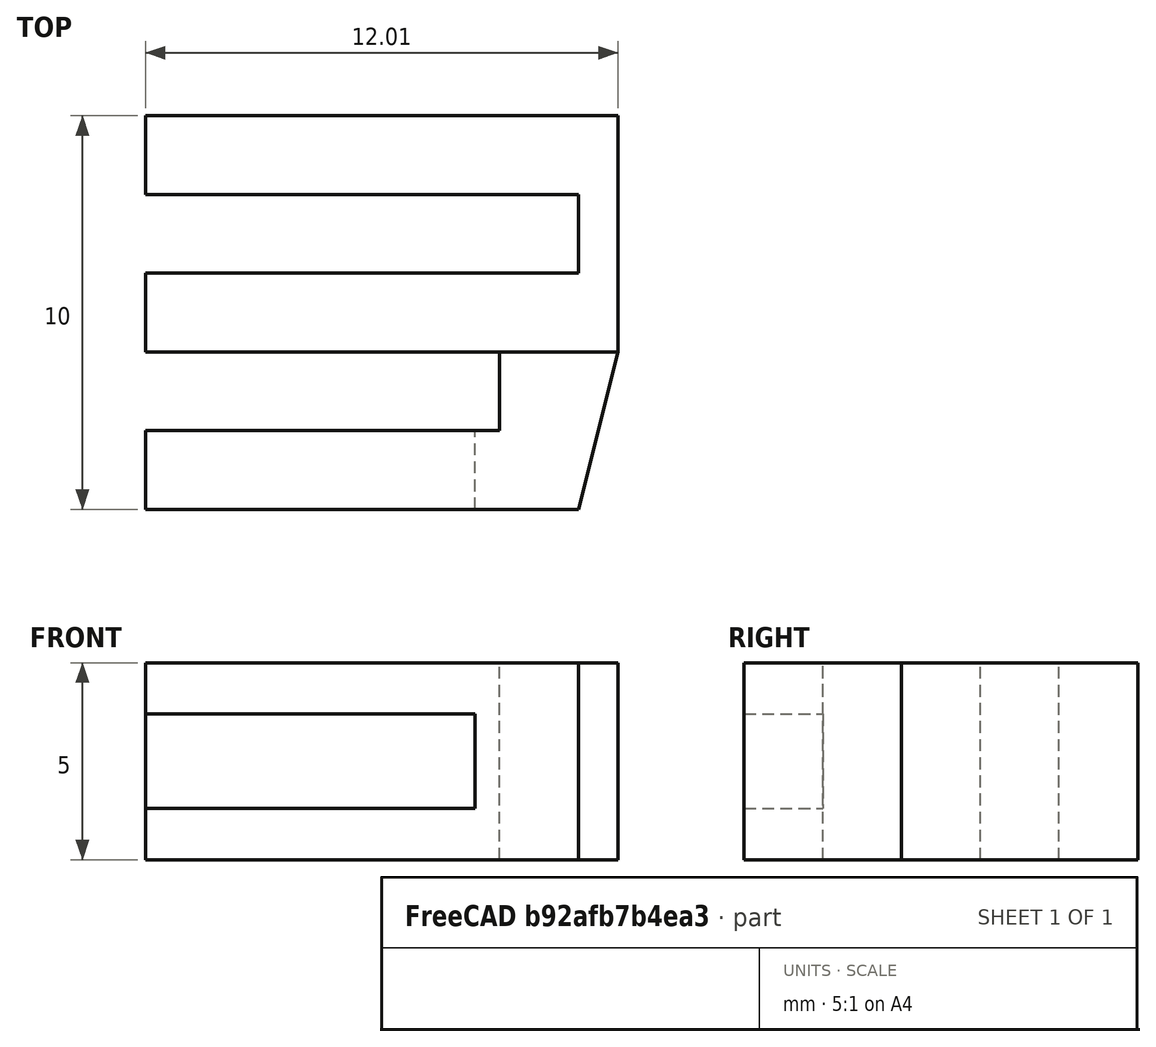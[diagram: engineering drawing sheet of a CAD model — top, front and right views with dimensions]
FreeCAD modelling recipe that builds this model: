
FCSTD DOCUMENT  (FreeCAD 0.18R16131 (Git))
Label: supportRegulateur
License: All rights reserved
LicenseURL: http://en.wikipedia.org/wiki/All_rights_reserved
objects: TechDraw::DrawProjGroupItem×4, Sketcher::SketchObject×3, Part::Extrusion×2, PartDesign::Pad×1, PartDesign::ShapeBinder×1, PartDesign::Plane×1, PartDesign::Body×1, Part::Cut×1, TechDraw::DrawSVGTemplate×1, TechDraw::DrawProjGroup×1, TechDraw::DrawViewDimension×1, TechDraw::DrawPage×1
note: 11 computed .brp shape members not serialized (recipe doc carries the construction recipe); baked Part::Feature solids carry a one-line shape summary decoded from their .brp

FEATURE [Sketcher::SketchObject] Sketch
  MapMode = 5
  Support = -> [XY_Plane]
  sketch-geometry (8):
    g0: LineSegment StartX=-12 StartY=6 StartZ=0 EndX=0 EndY=6 EndZ=0
    g1: LineSegment StartX=0 StartY=6 StartZ=0 EndX=0 EndY=0 EndZ=0
    g2: LineSegment StartX=0 StartY=0 StartZ=0 EndX=-12 EndY=0 EndZ=0
    g3: LineSegment StartX=-12 StartY=0 StartZ=0 EndX=-12 EndY=2 EndZ=0
    g4: LineSegment StartX=-12 StartY=2 StartZ=0 EndX=-1 EndY=2 EndZ=0
    g5: LineSegment StartX=-1 StartY=4 StartZ=0 EndX=-12 EndY=4 EndZ=0
    g6: LineSegment StartX=-12 StartY=4 StartZ=0 EndX=-12 EndY=6 EndZ=0
    g7: LineSegment StartX=-1 StartY=4 StartZ=0 EndX=-1 EndY=2 EndZ=0
  constraints (23):
    c: Horizontal(g0)
    c: Coincident(g0,g1)
    c: Vertical(g1)
    c: Coincident(g1,g2)
    c: Horizontal(g2)
    c: Coincident(g2,g3)
    c: Coincident(g3,g4)
    c: Horizontal(g4)
    c: Horizontal(g5)
    c: Coincident(g5,g6)
    c: Coincident(g6,g0)
    c: Vertical(g6)
    c: DistanceY(g6,g6) = 2
    c: Vertical(g3)
    c: DistanceY(g3,g3) = 2
    c: DistanceX(g5,g0) = 1
    c: DistanceY(g4,g5) = 2
    c: Equal(g5,g4)
    c: DistanceX(g0,g0) = 12
    c: Coincident(g-1,g1)
    c: Coincident(g7,g5)
    c: Coincident(g7,g4)
    c: Vertical(g7)
FEATURE [PartDesign::Pad] Pad
  Length = 5
  Length2 = 100
  Profile = -> Sketch
  Type = 0
FEATURE [Sketcher::SketchObject] Sketch001
  AttachmentOffset = pos=(-1,0,0) rot=(0,0,1;0rad)
  ExternalGeometry = -> [Sketch]
  MapMode = 5
  Placement = pos=(-1,0,0) rot=(0,0,1;0rad)
  Support = -> [XY_Plane]
  sketch-geometry (6):
    g0: LineSegment StartX=-2 StartY=0 StartZ=0 EndX=-2 EndY=-2 EndZ=0
    g1: LineSegment StartX=-2 StartY=-2 StartZ=0 EndX=-11 EndY=-2 EndZ=0
    g2: LineSegment StartX=-11 StartY=-2 StartZ=0 EndX=-11 EndY=-4 EndZ=0
    g3: LineSegment StartX=-11 StartY=-4 StartZ=0 EndX=0 EndY=-4 EndZ=0
    g4: LineSegment StartX=0 StartY=-4 StartZ=0 EndX=1.00622 EndY=0.002421 EndZ=0
    g5: LineSegment StartX=-2 StartY=0 StartZ=0 EndX=1.00622 EndY=0.002421 EndZ=0
  constraints (16):
    c: Vertical(g0)
    c: Coincident(g0,g1)
    c: Horizontal(g1)
    c: Coincident(g1,g2)
    c: Vertical(g2)
    c: Coincident(g2,g3)
    c: Horizontal(g3)
    c: Coincident(g3,g4)
    c: DistanceY(g0,g0) = 2
    c: DistanceX(g3,g3) = 11
    c: PointOnObject(g0,g-1)
    c: Coincident(g5,g0)
    c: DistanceX(g0,g3) = 2
    c: Coincident(g5,g4)
    c: PointOnObject(g3,g-2)
    c: DistanceY(g2,g2) = 2
FEATURE [Part::Extrusion] Extrude
  Base = -> Sketch001
  Dir = (0,0,1)
  DirMode = 2
  FaceMakerClass = Part::FaceMakerBullseye
  LengthFwd = 5
  LengthRev = 0
  Solid = true
  Symmetric = false
FEATURE [PartDesign::ShapeBinder] ReferenceExtrude
  Support = -> [Extrude]
  TraceSupport = false
FEATURE [PartDesign::Plane] DatumPlane
  Length = 26.1952
  MapMode = 5
  Placement = pos=(0,-4,0) rot=(1,0,0;1.5708rad)
  ResizeMode = 0
  Support = -> [ReferenceExtrude]
  Width = 24.1952
FEATURE [Sketcher::SketchObject] Sketch002
  ExternalGeometry = -> [ReferenceExtrude]
  MapMode = 5
  Placement = pos=(0,-4,0) rot=(1,0,0;1.5708rad)
  Support = -> [DatumPlane]
  sketch-geometry (5):
    g0: LineSegment StartX=-12 StartY=3.7 StartZ=0 EndX=-3.6304 EndY=3.7 EndZ=0
    g1: LineSegment StartX=-3.6304 StartY=3.7 StartZ=0 EndX=-3.6304 EndY=1.3 EndZ=0
    g2: LineSegment StartX=-3.6304 StartY=1.3 StartZ=0 EndX=-12 EndY=1.3 EndZ=0
    g3: LineSegment StartX=-12 StartY=1.3 StartZ=0 EndX=-12 EndY=3.7 EndZ=0
    g4: LineSegment [constr] StartX=-12 StartY=2.5 StartZ=0 EndX=6.57066 EndY=2.5 EndZ=0
  constraints (12):
    c: Coincident(g0,g1)
    c: Coincident(g1,g2)
    c: Coincident(g2,g3)
    c: Coincident(g3,g0)
    c: Horizontal(g0)
    c: Horizontal(g2)
    c: Vertical(g1)
    c: Vertical(g3)
    c: PointOnObject(g0,g-3)
    c: DistanceY(g1,g1) = 2.4
    c: Symmetric(g-3,g-3,g4)
    c: Symmetric(g0,g2,g4)
FEATURE [PartDesign::Body] Body
  Group = -> [Sketch,Pad,Sketch001,DatumPlane,ReferenceExtrude,Sketch002]
  Origin = -> Origin
  Tip = -> Pad
FEATURE [Part::Extrusion] Extrude001
  Base = -> Sketch002
  Dir = (0,-1,2e-16)
  DirMode = 2
  FaceMakerClass = Part::FaceMakerBullseye
  LengthFwd = 3
  LengthRev = 0
  Reversed = true
  Solid = true
  Symmetric = false
FEATURE [Part::Cut] Cut
  Base = -> Extrude
  Tool = -> Extrude001
FEATURE [TechDraw::DrawSVGTemplate] Template
  EditableTexts = Designed_by_Name=Designed by Name; Drawing_number=Drawing number; FC-Date=Date; FC-SC=Scale; FC-SH=Sheet; FC-Title=Title; Subtitle=Subtitle; Weight=Weight
  Height = 210
  Orientation = 1
  Width = 297
FEATURE [TechDraw::DrawProjGroupItem] ProjItem  label="Front"
  CoarseView = false
  Direction = (0,0,-1)
  Focus = 100
  HardHidden = false
  IsoCount = 0
  IsoHidden = false
  IsoVisible = false
  LockPosition = true
  Perspective = false
  Rotation = 0
  RotationVector = (1,0,0)
  Scale = 3
  ScaleType = 2
  SeamHidden = false
  SeamVisible = false
  SmoothHidden = false
  SmoothVisible = false
  Source = -> [Cut,Pad]
  Type = 0
  X = 0
  Y = 0
FEATURE [TechDraw::DrawProjGroupItem] ProjItem001  label="FrontBottomLeft"
  CoarseView = false
  Direction = (-1,1,-1)
  Focus = 100
  HardHidden = false
  IsoCount = 0
  IsoHidden = false
  IsoVisible = false
  LockPosition = false
  Perspective = false
  Rotation = 0
  RotationVector = (1,0,-1)
  Scale = 3
  ScaleType = 2
  SeamHidden = false
  SeamVisible = false
  SmoothHidden = false
  SmoothVisible = false
  Source = -> [Cut,Pad]
  Type = 8
  X = 60.3156
  Y = 60.3156
FEATURE [TechDraw::DrawProjGroupItem] ProjItem002  label="Bottom"
  CoarseView = false
  Direction = (0,1,0)
  Focus = 100
  HardHidden = false
  IsoCount = 0
  IsoHidden = false
  IsoVisible = false
  LockPosition = false
  Perspective = false
  Rotation = 0
  RotationVector = (1,0,0)
  Scale = 3
  ScaleType = 2
  SeamHidden = false
  SeamVisible = false
  SmoothHidden = false
  SmoothVisible = false
  Source = -> [Cut,Pad]
  Type = 5
  X = 0
  Y = 60.3156
FEATURE [TechDraw::DrawProjGroupItem] ProjItem003  label="Top"
  CoarseView = false
  Direction = (0,-1,0)
  Focus = 100
  HardHidden = false
  IsoCount = 0
  IsoHidden = false
  IsoVisible = false
  LockPosition = false
  Perspective = false
  Rotation = 0
  RotationVector = (1,0,0)
  Scale = 3
  ScaleType = 2
  SeamHidden = false
  SeamVisible = false
  SmoothHidden = false
  SmoothVisible = false
  Source = -> [Cut,Pad]
  Type = 4
  X = 0
  Y = -60.3156
FEATURE [TechDraw::DrawProjGroup] ProjGroup
  Anchor = -> ProjItem
  AutoDistribute = true
  LockPosition = false
  ProjectionType = 0
  Rotation = 0
  Scale = 3
  ScaleType = 2
  Source = -> [Cut,Pad]
  Views = -> [ProjItem,ProjItem001,ProjItem002,ProjItem003]
  X = 93.7602
  Y = 109.543
  spacingX = 15
  spacingY = 15
FEATURE [TechDraw::DrawViewDimension] Dimension
  Arbitrary = false
  FormatSpec = %.2f
  LockPosition = false
  MeasureType = 1
  OverTolerance = 0
  References2D = -> [ProjItem002]
  Rotation = 0
  ScaleType = 0
  Type = 2
  UnderTolerance = 0
  X = 43.8935
  Y = -24.0764
FEATURE [TechDraw::DrawPage] Page
  KeepUpdated = true
  ProjectionType = 0
  Template = -> Template
  Views = -> [ProjGroup,Dimension]
